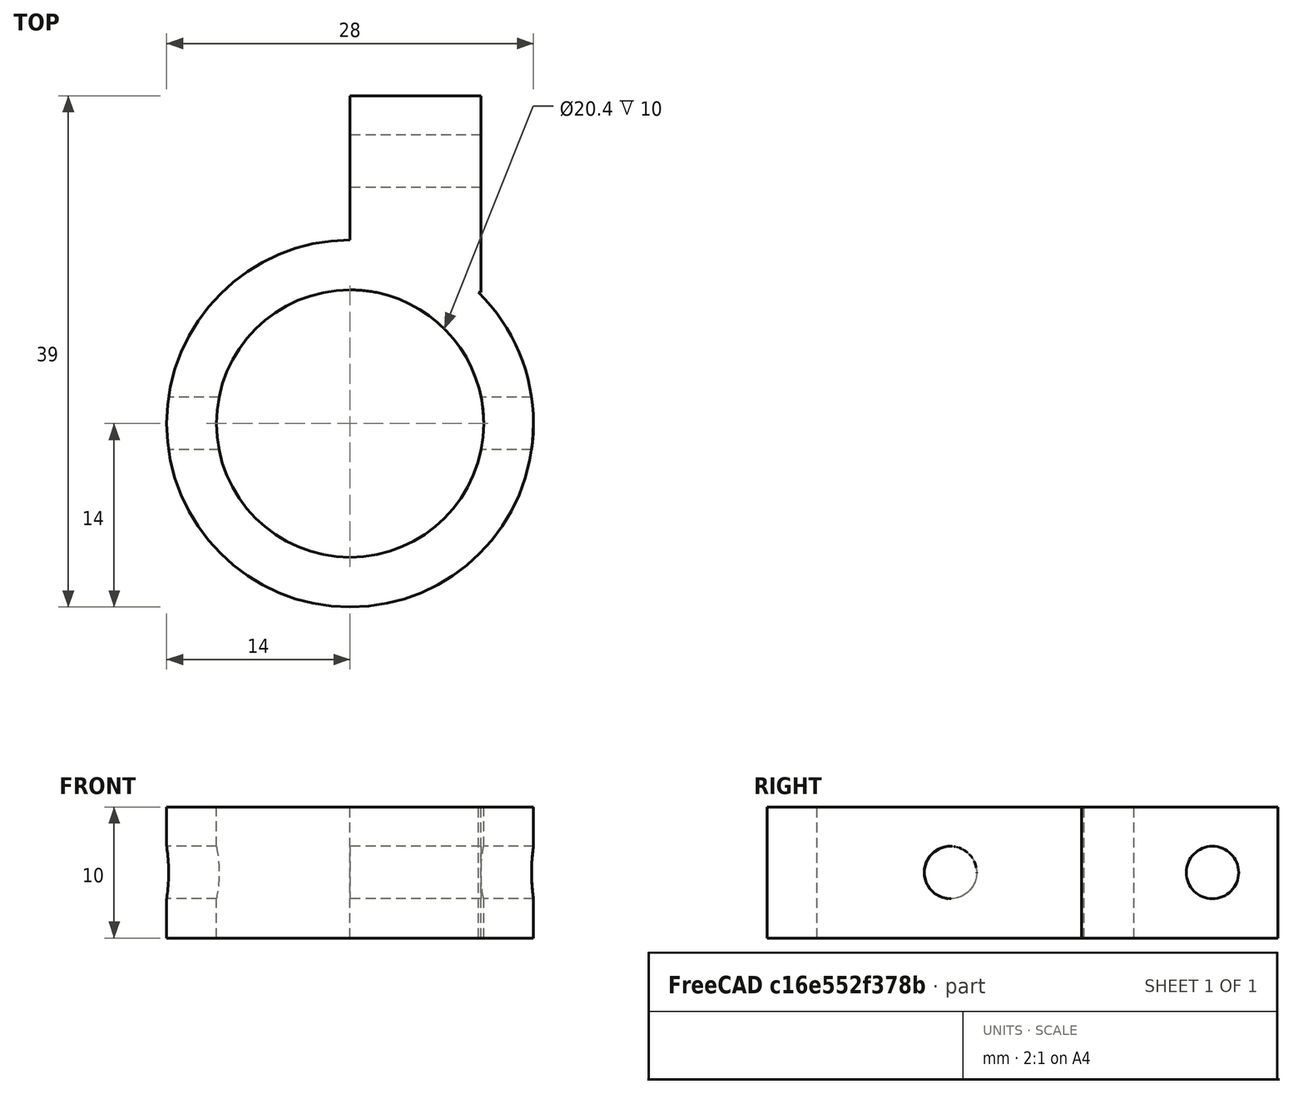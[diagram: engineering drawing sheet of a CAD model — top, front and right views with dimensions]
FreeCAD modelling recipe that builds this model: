
FCSTD DOCUMENT  (FreeCAD 0.17R13522 (Git))
Label: connector-attachment
License: All rights reserved
LicenseURL: http://en.wikipedia.org/wiki/All_rights_reserved
objects: Part::Cylinder×4, Part::MultiFuse×2, Part::Box×1, Part::Cut×1
note: 8 computed .brp shape members not serialized (recipe doc carries the construction recipe); baked Part::Feature solids carry a one-line shape summary decoded from their .brp

FEATURE [Part::Cylinder] Cylinder
  Angle = 360
  AttacherType = Attacher::AttachEngine3D
  Height = 10
  Placement = pos=(0,0,-5) rot=(0,0,1;0rad)
  Radius = 14
FEATURE [Part::Cylinder] Cylinder001
  Angle = 360
  AttacherType = Attacher::AttachEngine3D
  Height = 10
  Placement = pos=(0,0,-5) rot=(0,0,1;0rad)
  Radius = 10.2
FEATURE [Part::Box] Box  label="Cube"
  AttacherType = Attacher::AttachEngine3D
  Height = 10
  Length = 10
  Placement = pos=(0,10,-5) rot=(0,0,1;0rad)
  Width = 15
FEATURE [Part::Cylinder] Cylinder003
  Angle = 360
  AttacherType = Attacher::AttachEngine3D
  Height = 10
  Placement = pos=(10,20,0) rot=(0,-1,0;1.5708rad)
  Radius = 2
FEATURE [Part::MultiFuse] Fusion001  label="Positive Fusion"
  Shapes = -> [Cylinder,Box]
FEATURE [Part::Cylinder] Cylinder004
  Angle = 360
  AttacherType = Attacher::AttachEngine3D
  Height = 30
  Placement = pos=(15,0,0) rot=(0,-1,0;1.5708rad)
  Radius = 2
FEATURE [Part::MultiFuse] Fusion  label="Negative Fusion"
  Shapes = -> [Cylinder001,Cylinder003,Cylinder004]
FEATURE [Part::Cut] Cut
  Base = -> Fusion001
  Tool = -> Fusion
